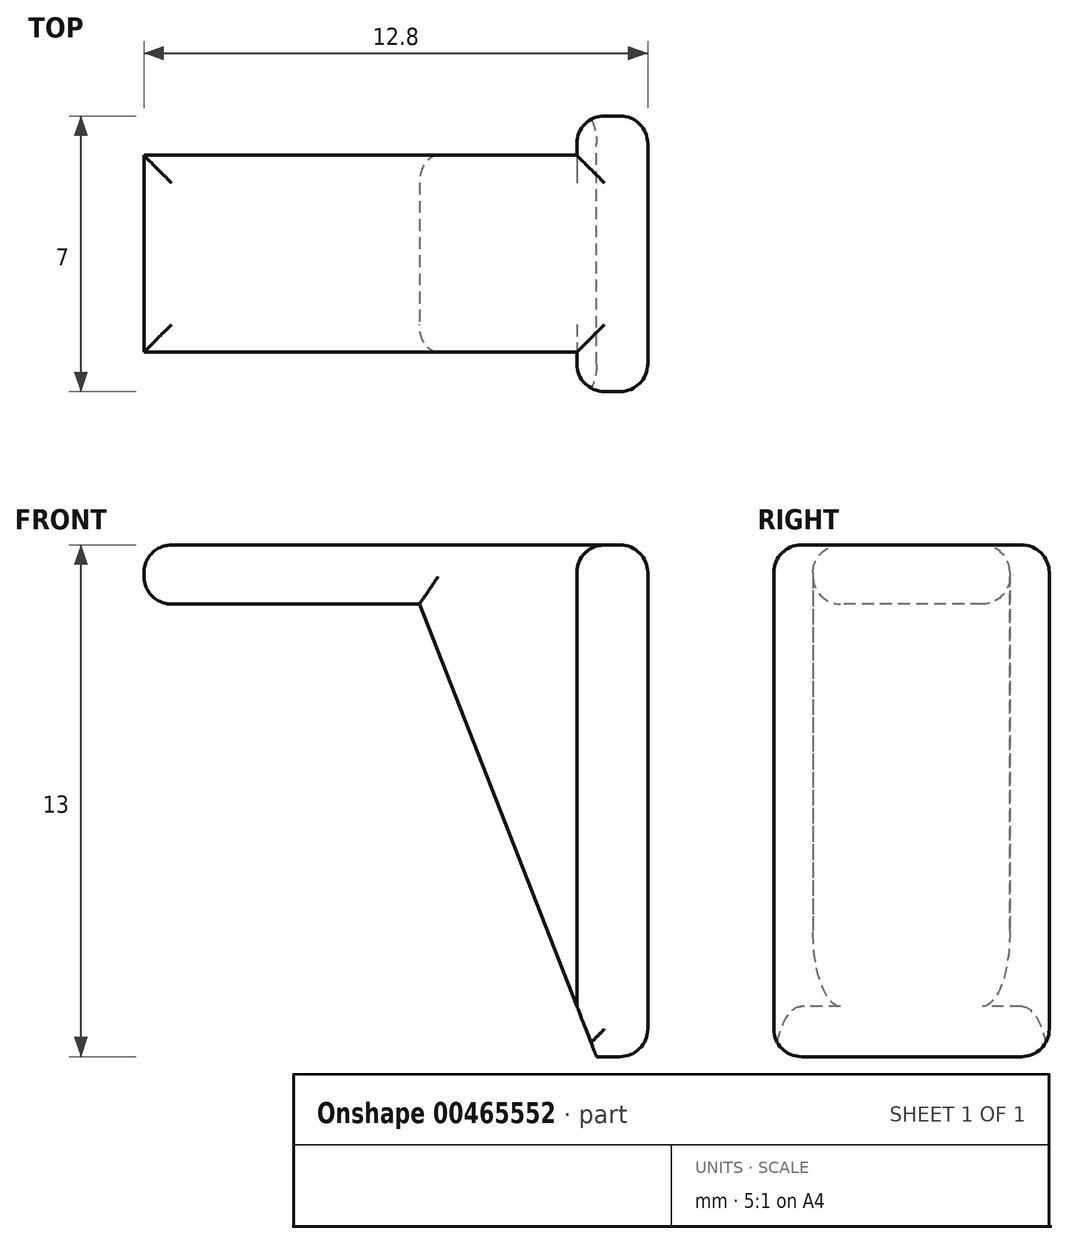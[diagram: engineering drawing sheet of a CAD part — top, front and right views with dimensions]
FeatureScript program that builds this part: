
annotation { "Feature Type Name" : "Feature", "Feature Type Description" : "" }
export const myFeature = defineFeature(function(context is Context, id is Id, definition is map)
    precondition{}
    {
        {
            var Q0;
            Q0=qCreatedBy(makeId("Top.planeOp"),FACE);
            var sketch = newSketch(context, id + "F0", { "sketchPlane" : qUnion([Q0])});
            skLineSegment(sketch, "E0", {"start": v(-1, 5) * mm, "end": v(3, 5) * mm});
            skLineSegment(sketch, "E1", {"start": v(3, 5) * mm, "end": v(3, 6) * mm});
            skLineSegment(sketch, "E2", {"start": v(3, 6) * mm, "end": v(4.8, 6) * mm});
            skLineSegment(sketch, "E3", {"start": v(4.8, 6) * mm, "end": v(4.8, -1) * mm});
            skLineSegment(sketch, "E4", {"start": v(4.8, -1) * mm, "end": v(3, -1) * mm});
            skLineSegment(sketch, "E5", {"start": v(3, -1) * mm, "end": v(3, 0) * mm});
            skLineSegment(sketch, "E6", {"start": v(3, 0) * mm, "end": v(-1, 0) * mm});
            skLineSegment(sketch, "E7", {"start": v(-1, 0) * mm, "end": v(-1, 5) * mm});
            skSolve(sketch);
        }
        {
            var Q0;
            Q0 = qSketchRegion(id + "F0", true);
            extrude(context, id + "F1", {"entities" : qUnion([Q0]), "depth" : 13 * mm});
        }
        {
            var Q0;
            Q0=qCreatedBy(makeId("Front.planeOp"),FACE);
            var sketch = newSketch(context, id + "F2", { "sketchPlane" : qUnion([Q0])});
            skLineSegment(sketch, "E8.bottom", {"start": v(-8, 13) * mm, "end": v(0, 13) * mm});
            skLineSegment(sketch, "E8.top", {"start": v(-8, 11.5) * mm, "end": v(0, 11.5) * mm});
            skLineSegment(sketch, "E8.left", {"start": v(-8, 13) * mm, "end": v(-8, 11.5) * mm});
            skLineSegment(sketch, "E8.right", {"start": v(0, 13) * mm, "end": v(0, 11.5) * mm});
            skSolve(sketch);
        }
        {
            var Q0;
            Q0 = qSketchRegion(id + "F2", true);
            extrude(context, id + "F3", {"entities" : qUnion([Q0]), "operationType" : NewBodyOperationType.ADD, "oppositeDirection" : true, "depth" : 5 * mm});
        }
        {
            var Q0;
            Q0=makeQuery(id+"F1.opExtrude","CAP_EDGE",EDGE,{"disambiguationData":[OSD([sQuery(id+"F0.wireOp",EDGE,"E7")])],"isStart":true});
            chamfer(context, id + "F4", {"entities" : qUnion([Q0]), "chamferType" : ChamferType.TWO_OFFSETS, "width1" : 4.5 * mm, "oppositeDirection" : false, "width2" : 11.5 * mm, "tangentPropagation" : true});
        }
        {
            var Q0;
            Q0=makeQuery(id+"F1.opExtrude","SWEPT_EDGE",EDGE,{"disambiguationData":[OSD([sQuery(id+"F0.wireOp",EDGE,"E2"),sQuery(id+"F0.wireOp",EDGE,"E3")])]});
            var Q1;
            Q1=makeQuery(id+"F1.opExtrude","SWEPT_EDGE",EDGE,{"disambiguationData":[OSD([sQuery(id+"F0.wireOp",EDGE,"E1"),sQuery(id+"F0.wireOp",EDGE,"E2")])]});
            var Q2;
            Q2=makeQuery(id+"F1.opExtrude","SWEPT_EDGE",EDGE,{"disambiguationData":[OSD([sQuery(id+"F0.wireOp",EDGE,"E3"),sQuery(id+"F0.wireOp",EDGE,"E4")])]});
            var Q3;
            Q3=makeQuery(id+"F1.opExtrude","SWEPT_EDGE",EDGE,{"disambiguationData":[OSD([sQuery(id+"F0.wireOp",EDGE,"E4"),sQuery(id+"F0.wireOp",EDGE,"E5")])]});
            var Q4;
            Q4=makeQuery(id+"F1.opExtrude","CAP_EDGE",EDGE,{"disambiguationData":[OSD([sQuery(id+"F0.wireOp",EDGE,"E3")])],"isStart":false});
            var Q5;
            Q5=makeQuery(id+"F3.boolean.opBoolean","MERGE",EDGE,{"derivedFrom":[makeQuery(id+"F1.opExtrude","CAP_EDGE",EDGE,{"disambiguationData":[OSD([sQuery(id+"F0.wireOp",EDGE,"E6")])],"isStart":false}),makeQuery(id+"F3.opExtrude","CAP_EDGE",EDGE,{"disambiguationData":[OSD([sQuery(id+"F2.wireOp",EDGE,"E8.bottom")])],"isStart":true})]});
            var Q6;
            Q6=makeQuery(id+"F1.opExtrude","CAP_EDGE",EDGE,{"disambiguationData":[OSD([sQuery(id+"F0.wireOp",EDGE,"E4")])],"isStart":false});
            var Q7;
            Q7=makeQuery(id+"F1.opExtrude","CAP_EDGE",EDGE,{"disambiguationData":[OSD([sQuery(id+"F0.wireOp",EDGE,"E2")])],"isStart":false});
            var Q8;
            Q8=makeQuery(id+"F1.opExtrude","CAP_EDGE",EDGE,{"disambiguationData":[OSD([sQuery(id+"F0.wireOp",EDGE,"E5")])],"isStart":false});
            var Q9;
            Q9=makeQuery(id+"F1.opExtrude","CAP_EDGE",EDGE,{"disambiguationData":[OSD([sQuery(id+"F0.wireOp",EDGE,"E1")])],"isStart":false});
            var Q10;
            Q10=makeQuery(id+"F3.boolean.opBoolean","MERGE",EDGE,{"derivedFrom":[makeQuery(id+"F1.opExtrude","CAP_EDGE",EDGE,{"disambiguationData":[OSD([sQuery(id+"F0.wireOp",EDGE,"E0")])],"isStart":false}),makeQuery(id+"F3.opExtrude","CAP_EDGE",EDGE,{"disambiguationData":[OSD([sQuery(id+"F2.wireOp",EDGE,"E8.bottom")])],"isStart":false})]});
            var Q11;
            Q11=makeQuery(id+"F3.opExtrude","SWEPT_EDGE",EDGE,{"disambiguationData":[OSD([sQuery(id+"F2.wireOp",EDGE,"E8.bottom"),sQuery(id+"F2.wireOp",EDGE,"E8.left")])]});
            var Q12;
            Q12=makeQuery(id+"F3.opExtrude","SWEPT_EDGE",EDGE,{"disambiguationData":[OSD([sQuery(id+"F2.wireOp",EDGE,"E8.top"),sQuery(id+"F2.wireOp",EDGE,"E8.left")])]});
            var Q13;
            Q13=makeQuery(id+"F1.opExtrude","CAP_EDGE",EDGE,{"disambiguationData":[OSD([sQuery(id+"F0.wireOp",EDGE,"E3")])],"isStart":true});
            var Q14;
            Q14=makeQuery(id+"F1.opExtrude","CAP_EDGE",EDGE,{"disambiguationData":[OSD([sQuery(id+"F0.wireOp",EDGE,"E4")])],"isStart":true});
            var Q15;
            Q15=makeQuery(id+"F1.opExtrude","CAP_EDGE",EDGE,{"disambiguationData":[OSD([sQuery(id+"F0.wireOp",EDGE,"E2")])],"isStart":true});
            var Q16;
            Q16=makeQuery(id+"F1.opExtrude","CAP_EDGE",EDGE,{"disambiguationData":[OSD([sQuery(id+"F0.wireOp",EDGE,"E5")])],"isStart":true});
            var Q17;
            Q17=makeQuery(id+"F1.opExtrude","CAP_EDGE",EDGE,{"disambiguationData":[OSD([sQuery(id+"F0.wireOp",EDGE,"E1")])],"isStart":true});
            var Q18;
            Q18=makeQuery(id+"F3.opExtrude","CAP_EDGE",EDGE,{"disambiguationData":[OSD([sQuery(id+"F2.wireOp",EDGE,"E8.top")])],"isStart":true});
            var Q19;
            Q19=makeQuery(id+"F3.opExtrude","CAP_EDGE",EDGE,{"disambiguationData":[OSD([sQuery(id+"F2.wireOp",EDGE,"E8.top")])],"isStart":false});
            var Q20;
            Q20=makeQuery(id+"F4.opChamfer","BLEND_EDGE",EDGE,{"blendedFrom":[makeQuery(id+"F1.opExtrude","CAP_EDGE",EDGE,{"disambiguationData":[OSD([sQuery(id+"F0.wireOp",EDGE,"E7")])],"isStart":true}),makeQuery(id+"F3.boolean.opBoolean","MERGE",FACE,{"derivedFrom":[makeQuery(id+"F1.opExtrude","SWEPT_FACE",FACE,{"disambiguationData":[OSD([sQuery(id+"F0.wireOp",EDGE,"E6")])]}),makeQuery(id+"F3.opExtrude","CAP_FACE",FACE,{"disambiguationData":[OSD([sQuery(id+"F2.wireOp",EDGE,"E8.bottom"),sQuery(id+"F2.wireOp",EDGE,"E8.top"),sQuery(id+"F2.wireOp",EDGE,"E8.left"),sQuery(id+"F2.wireOp",EDGE,"E8.right")])],"isStart":true})]})],"blendedInto":[makeQuery(id+"F3.boolean.opBoolean","MERGE",FACE,{"derivedFrom":[makeQuery(id+"F1.opExtrude","SWEPT_FACE",FACE,{"disambiguationData":[OSD([sQuery(id+"F0.wireOp",EDGE,"E6")])]}),makeQuery(id+"F3.opExtrude","CAP_FACE",FACE,{"disambiguationData":[OSD([sQuery(id+"F2.wireOp",EDGE,"E8.bottom"),sQuery(id+"F2.wireOp",EDGE,"E8.top"),sQuery(id+"F2.wireOp",EDGE,"E8.left"),sQuery(id+"F2.wireOp",EDGE,"E8.right")])],"isStart":true})]})]});
            var Q21;
            Q21=makeQuery(id+"F4.opChamfer","BLEND_EDGE",EDGE,{"blendedFrom":[makeQuery(id+"F1.opExtrude","CAP_EDGE",EDGE,{"disambiguationData":[OSD([sQuery(id+"F0.wireOp",EDGE,"E7")])],"isStart":true}),makeQuery(id+"F3.boolean.opBoolean","MERGE",FACE,{"derivedFrom":[makeQuery(id+"F1.opExtrude","SWEPT_FACE",FACE,{"disambiguationData":[OSD([sQuery(id+"F0.wireOp",EDGE,"E0")])]}),makeQuery(id+"F3.opExtrude","CAP_FACE",FACE,{"disambiguationData":[OSD([sQuery(id+"F2.wireOp",EDGE,"E8.bottom"),sQuery(id+"F2.wireOp",EDGE,"E8.top"),sQuery(id+"F2.wireOp",EDGE,"E8.left"),sQuery(id+"F2.wireOp",EDGE,"E8.right")])],"isStart":false})]})],"blendedInto":[makeQuery(id+"F3.boolean.opBoolean","MERGE",FACE,{"derivedFrom":[makeQuery(id+"F1.opExtrude","SWEPT_FACE",FACE,{"disambiguationData":[OSD([sQuery(id+"F0.wireOp",EDGE,"E0")])]}),makeQuery(id+"F3.opExtrude","CAP_FACE",FACE,{"disambiguationData":[OSD([sQuery(id+"F2.wireOp",EDGE,"E8.bottom"),sQuery(id+"F2.wireOp",EDGE,"E8.top"),sQuery(id+"F2.wireOp",EDGE,"E8.left"),sQuery(id+"F2.wireOp",EDGE,"E8.right")])],"isStart":false})]})]});
            fillet(context, id + "F5", {"entities" : qUnion([Q0, Q1, Q2, Q3, Q4, Q5, Q6, Q7, Q8, Q9, Q10, Q11, Q12, Q13, Q14, Q15, Q16, Q17, Q18, Q19, Q20, Q21]), "radius" : 0.7 * mm, "tangentPropagation" : true, "allowEdgeOverflow" : false});
        }
    });
